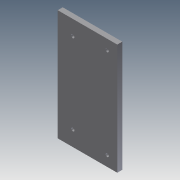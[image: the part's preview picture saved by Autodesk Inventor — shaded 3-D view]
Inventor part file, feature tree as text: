
AUTODESK INVENTOR PART (.ipt)
format: ipt  version: 2011 (Build 150239000, 239)  size: 131,072 bytes
history: native  units: in
note: dims shown in document units (in); Inventor stores cm internally (conversion verified against a paired STEP export)
features: extrude x7, sketch x7
ambient origin geometry x8: Origin, YZ Plane, XZ Plane, XY Plane, X Axis, Y Axis, Z Axis, Center Point
bodies: Solid1 (feature_tree)
feature tree (14):
  extrude  "Extrusion1"  Depth=6.0in
  extrude  "Extrusion2"  Depth=0.5in
  extrude  "Extrusion3"  Depth=0.5in
  extrude  "Extrusion4"  Depth=0.75in
  extrude  "Extrusion5"  Depth=0.75in
  extrude  "Extrusion6"  Depth=0.5in
  extrude  "Extrusion7"  Depth=0.156in
  sketch  "Sketch1"  dims[d0=2.9528in d1=6.0in]
  sketch  "Sketch2"  dims[d2=0.25in d3=0.0in d4=0.5in]
  sketch  "Sketch3"  dims[d5=1.0in d6=0.0in d7=0.5in]
  sketch  "Sketch4"  dims[d8=0.5in d9=0.75in]
  sketch  "Sketch5"  dims[d10=0.75in d11=0.75in]
  sketch  "Sketch6"  dims[d12=0.5in d13=0.5in]
  sketch  "Sketch7"  dims[d14=0.156in d15=0.156in d16=1.0in d17=0.0in d18=0.25in d19=0.0in d20=3.0in d21=0.0in d22=5.5in d23=0.1in d24=0.0in d25=0.5in d26=0.5in d27=0.5in d28=0.5in d29=0.156in d30=0.156in d31=1.0in d32=0.0in]
